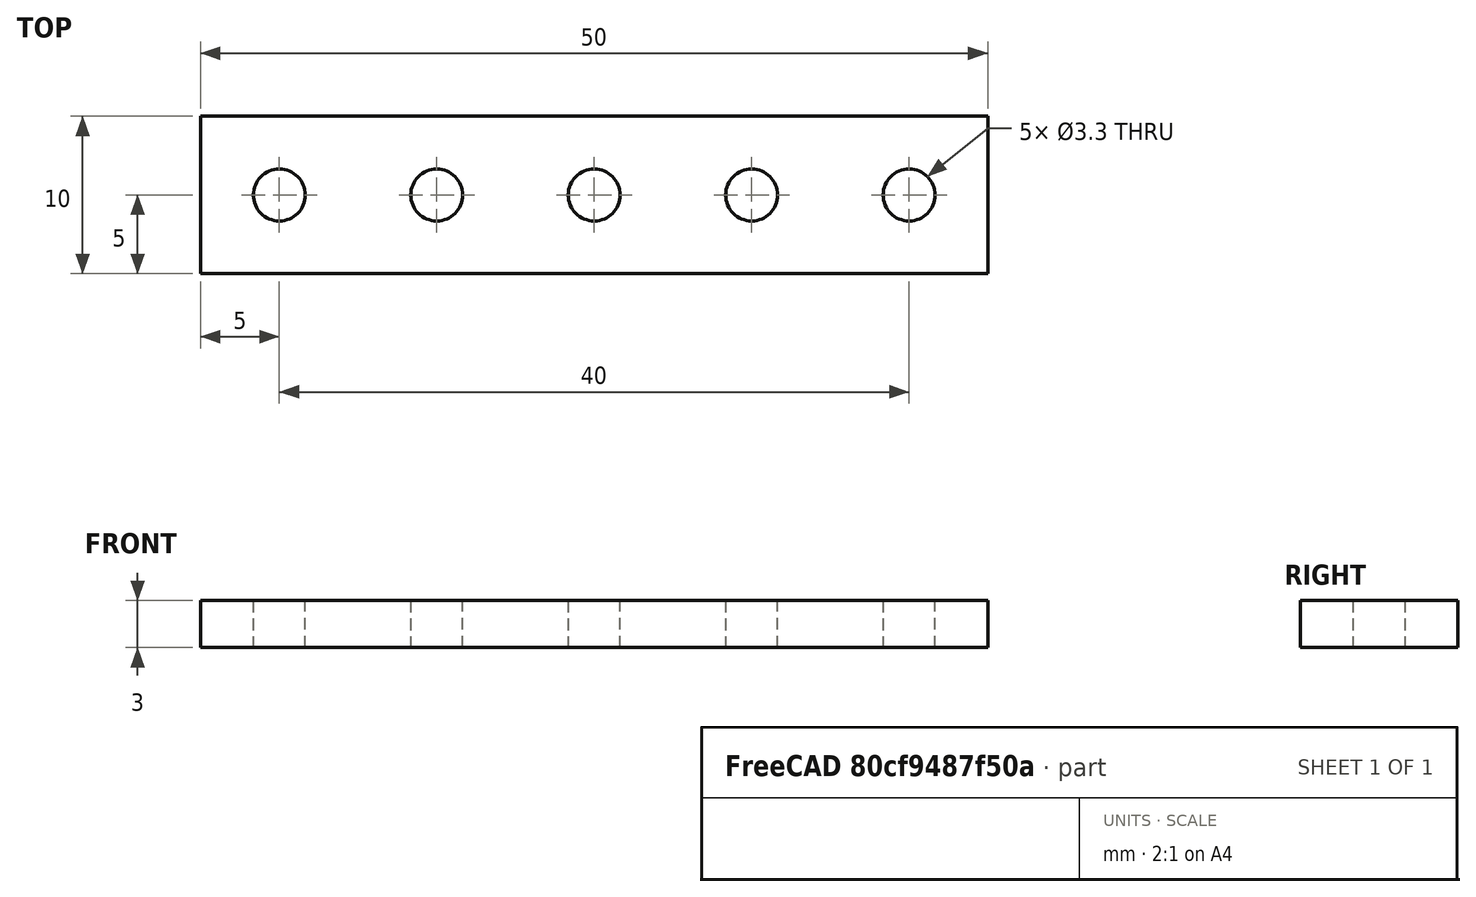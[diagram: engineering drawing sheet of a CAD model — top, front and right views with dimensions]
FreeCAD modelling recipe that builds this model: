
FCSTD DOCUMENT  (FreeCAD 0.20R29177 +426 (Git))
Label: pieza_mecano
License: Creative Commons Attribution-ShareAlike
LicenseURL: http://creativecommons.org/licenses/by-sa/4.0/
objects: Part::Extrusion×2, Sketcher::SketchObject×1
note: 3 computed .brp shape members not serialized (recipe doc carries the construction recipe); baked Part::Feature solids carry a one-line shape summary decoded from their .brp

FEATURE [Sketcher::SketchObject] Sketch
  FullyConstrained = true
  sketch-geometry (10):
    g0: LineSegment StartX=-25 StartY=-5 StartZ=0 EndX=-25 EndY=5 EndZ=0
    g1: LineSegment StartX=-25 StartY=5 StartZ=0 EndX=25 EndY=5 EndZ=0
    g2: LineSegment StartX=25 StartY=5 StartZ=0 EndX=25 EndY=-5 EndZ=0
    g3: LineSegment StartX=25 StartY=-5 StartZ=0 EndX=-25 EndY=-5 EndZ=0
    g4: GeomPoint X=0 Y=0 Z=0
    g5: Circle CenterX=0 CenterY=0 CenterZ=0 NormalX=0 NormalY=0 NormalZ=1 AngleXU=0 Radius=1.65
    g6: Circle CenterX=-10 CenterY=0 CenterZ=0 NormalX=0 NormalY=0 NormalZ=1 AngleXU=0 Radius=1.65
    g7: Circle CenterX=-20 CenterY=0 CenterZ=0 NormalX=0 NormalY=0 NormalZ=1 AngleXU=0 Radius=1.65
    g8: Circle CenterX=10 CenterY=0 CenterZ=0 NormalX=0 NormalY=0 NormalZ=1 AngleXU=0 Radius=1.65
    g9: Circle CenterX=20 CenterY=0 CenterZ=0 NormalX=0 NormalY=0 NormalZ=1 AngleXU=0 Radius=1.65
  constraints (24):
    c: Coincident(g0,g1)
    c: Coincident(g1,g2)
    c: Coincident(g2,g3)
    c: Coincident(g3,g0)
    c: Horizontal(g1)
    c: Horizontal(g3)
    c: Vertical(g0)
    c: Vertical(g2)
    c: Symmetric(g1,g0,g4)
    c: Coincident(g4,g-1)
    c: Distance(g1) = 50
    c: Distance(g2) = 10
    c: Coincident(g5,g4)
    c: Diameter(g5) = 3.3
    c: PointOnObject(g6,g-1)
    c: PointOnObject(g7,g-1)
    c: Distance(g6,g5) = 10
    c: Distance(g6,g7) = 10
    c: Diameter(g6) = 3.3
    c: Diameter(g7) = 3.3
    c: Diameter(g9) = 3.3
    c: Diameter(g8) = 3.3
    c: Symmetric(g9,g7,g-2)
    c: Symmetric(g8,g6,g-2)
FEATURE [Part::Extrusion] Extrude
  Base = -> Sketch
  Dir = (0,0,1)
  DirMode = 2
  FaceMakerClass = Part::FaceMakerBullseye
  LengthFwd = 3
  LengthRev = 0
  Solid = true
  Symmetric = false
FEATURE [Part::Extrusion] Extrude001
  Base = -> Sketch
  Dir = (0,0,1)
  DirMode = 2
  FaceMakerClass = Part::FaceMakerBullseye
  LengthFwd = 3
  LengthRev = 0
  Solid = true
  Symmetric = false
